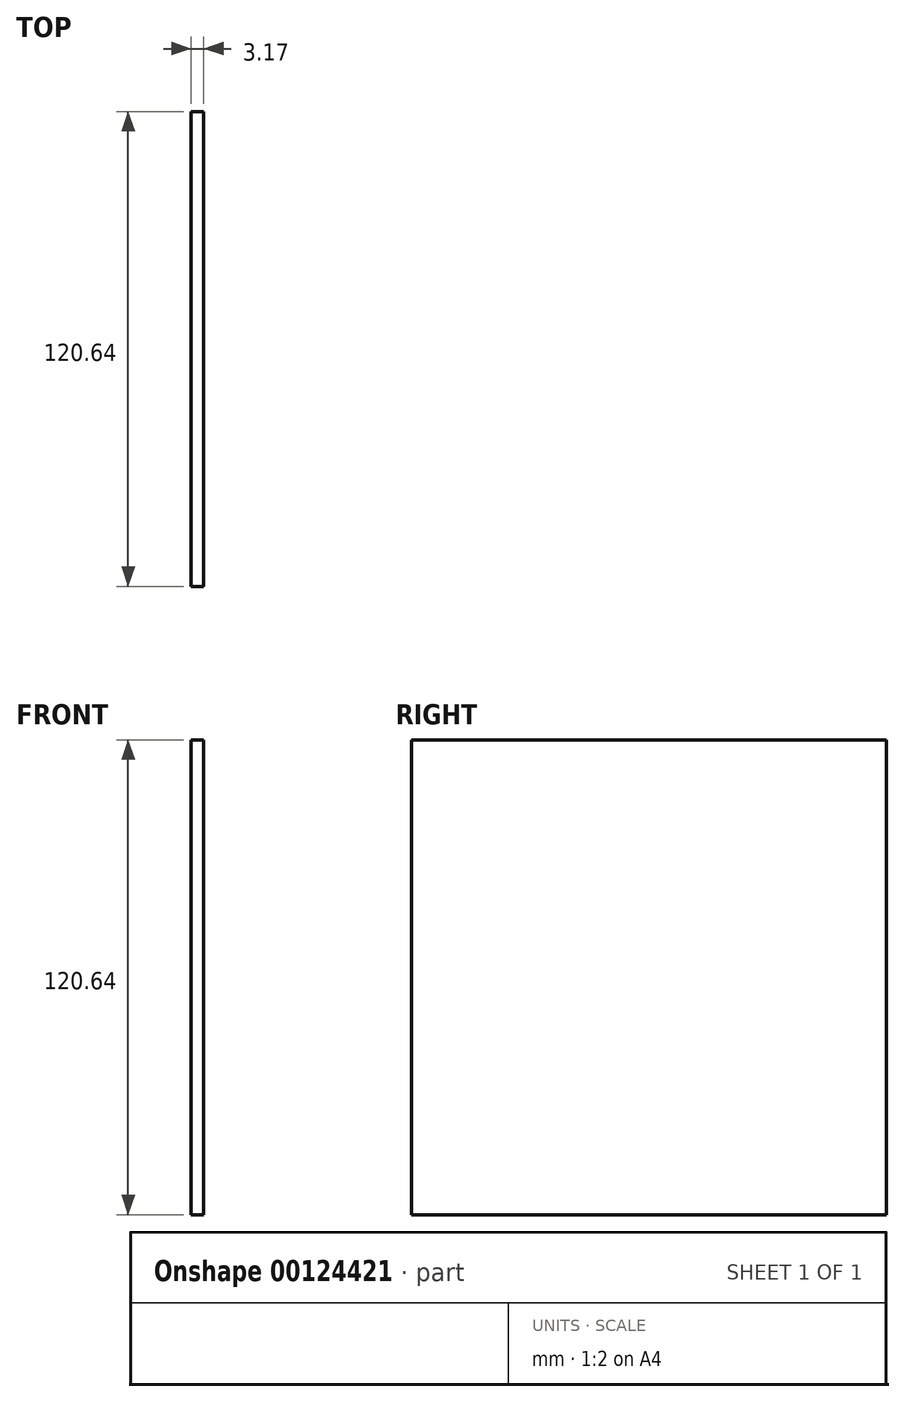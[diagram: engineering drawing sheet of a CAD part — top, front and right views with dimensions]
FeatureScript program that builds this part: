
annotation { "Feature Type Name" : "Feature", "Feature Type Description" : "" }
export const myFeature = defineFeature(function(context is Context, id is Id, definition is map)
    precondition{}
    {
        {
            var Q0;
            Q0=qCreatedBy(makeId("Right.planeOp"),FACE);
            var sketch = newSketch(context, id + "F0", { "sketchPlane" : qUnion([Q0])});
            skLineSegment(sketch, "E0.bottom", {"start": v(60.32, -60.33) * mm, "end": v(-60.33, -60.33) * mm});
            skLineSegment(sketch, "E0.top", {"start": v(60.33, 60.33) * mm, "end": v(-60.33, 60.33) * mm});
            skLineSegment(sketch, "E0.left", {"start": v(60.32, -60.33) * mm, "end": v(60.33, 60.32) * mm});
            skLineSegment(sketch, "E0.right", {"start": v(-60.33, -60.33) * mm, "end": v(-60.32, 60.32) * mm});
            skPoint(sketch, "E0.middle", {"position": v(0, 0) * mm});
            skSolve(sketch);
        }
        {
            var Q0;
            Q0 = qSketchRegion(id + "F0", true);
            extrude(context, id + "F1", {"entities" : qUnion([Q0]), "depth" : 3.17 * mm});
        }
    });
